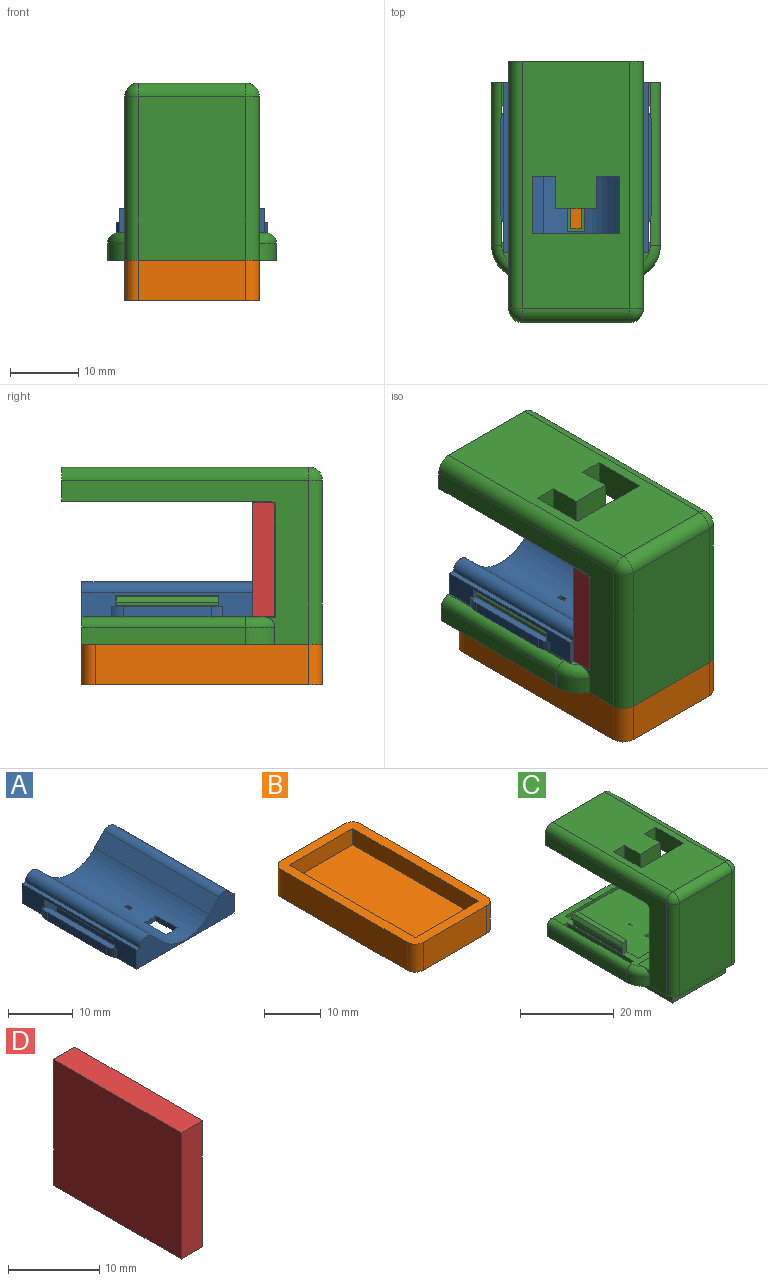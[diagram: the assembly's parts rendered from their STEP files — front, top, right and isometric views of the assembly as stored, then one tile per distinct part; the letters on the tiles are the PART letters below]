
ASSEMBLY  parts=4 mates=1
PART A: 50 faces, bbox 22.3x25x5.7 mm
  f0: plane 16.2x1.05mm, normal (0,0,1), area 15.9mm2, adj f2,f41,f42,f44,f45,f46,f47
  f1: plane 3.4x0.6mm, normal (1,0,0), area 2mm2, adj f5,f6,f13,f42
  f2: plane 25x3.64mm, normal (1,0,0), area 42.3mm2, adj f0,f6,f14,f15,f32,f40,f41,f42
  f3: plane 25x3.64mm, normal (-1,0,0), area 42.3mm2, adj f6,f14,f15,f31,f33,f34,f36,f37
  f4: plane 3.4x0.6mm, normal (-1,0,0), area 2mm2, adj f5,f6,f30,f34
  f5: plane 22x16.78mm, normal (0,0,-1), area 347.9mm2, adj f1,f4,f7,f8,f9,f10,f11,f12
  f6: plane 25x22.28mm, normal (0,0,-1), area 126.3mm2, adj f1,f2,f3,f4,f7,f8,f13,f14
  f7: plane 3.4x0.6mm, normal (-1,0,0), area 2mm2, adj f5,f6,f13,f33
  f8: plane 3.4x0.6mm, normal (1,0,0), area 2mm2, adj f5,f6,f30,f41
  f9: plane 0.55x0.39mm, normal (0,1,0), area 0.2mm2, adj f5,f10,f12,f27
  f10: plane 0.89x0.55mm, normal (-1,0,0), area 0.5mm2, adj f5,f9,f11,f27
  f11: plane 0.55x0.39mm, normal (0,-1,0), area 0.2mm2, adj f5,f10,f12,f27
  f12: plane 0.89x0.55mm, normal (1,0,0), area 0.5mm2, adj f5,f9,f11,f27
  f13: plane 16.78x0.6mm, normal (0,1,0), area 10.1mm2, adj f1,f5,f6,f7
  f14: plane 21.28x5.14mm, normal (0,1,0), area 56.1mm2, adj f2,f3,f6,f16,f17,f18,f28,f29
  f15: plane 21.28x5.14mm, normal (0,-1,0), area 56.1mm2, adj f2,f3,f6,f16,f17,f18,f28,f29
  f16: cylinder r=7mm len=25mm, axis (0,1,0), area 262.3mm2, adj f14,f15,f17,f18,f19,f20,f21,f22
  f17: plane 25x2.16mm, normal (-0.71,0,0.71), area 76.5mm2, adj f14,f15,f16,f29
  f18: plane 25x2.61mm, normal (0.71,0,0.71), area 92.1mm2, adj f14,f15,f16,f28
  f19: plane 4.7x0.97mm, normal (-1,0,0), area 4.6mm2, adj f5,f16,f20,f22
  f20: plane 2.5x0.97mm, normal (0,1,0), area 2.2mm2, adj f5,f16,f19,f21
  f21: plane 4.7x0.97mm, normal (1,0,0), area 4.6mm2, adj f5,f16,f20,f22
  f22: plane 2.5x0.97mm, normal (0,-1,0), area 2.2mm2, adj f5,f16,f19,f21
  f23: plane 1.15x0.32mm, normal (-1,0,0), area 0.4mm2, adj f16,f24,f26,f27
  f24: plane 0.65x0.32mm, normal (0,1,0), area 0.2mm2, adj f16,f23,f25,f27
  f25: plane 1.15x0.32mm, normal (1,0,0), area 0.4mm2, adj f16,f24,f26,f27
  f26: plane 0.65x0.32mm, normal (0,-1,0), area 0.2mm2, adj f16,f23,f25,f27
  f27: plane 1.15x0.65mm, normal (0,0,1), area 0.4mm2, adj f9,f10,f11,f12,f23,f24,f25,f26
  f28: cylinder r=1.5mm len=25mm, axis (0,1,0), area 88.4mm2, adj f14,f15,f18,f31
  f29: cylinder r=1.5mm len=25mm, axis (0,1,0), area 88.4mm2, adj f14,f15,f17,f32
  f30: plane 16.78x0.6mm, normal (0,-1,0), area 10.1mm2, adj f4,f5,f6,f8
  f31: plane 25x0.75mm, normal (0,0,1), area 18.8mm2, adj f3,f14,f15,f28
  f32: plane 25x0.75mm, normal (0,0,1), area 18.8mm2, adj f2,f14,f15,f29
  f33: plane 3.7x2.55mm, normal (0,-1,0), area 7.2mm2, adj f3,f5,f6,f7,f35,f36,f37,f38
  f34: plane 3.7x2.55mm, normal (0,1,0), area 7.2mm2, adj f3,f4,f5,f6,f35,f36,f37,f38
  f35: plane 15.2x1.55mm, normal (1,0,0), area 23.6mm2, adj f6,f33,f34,f37
  f36: plane 15.2x2.55mm, normal (0,0,-1), area 38.8mm2, adj f3,f33,f34,f38
  f37: plane 16.2x1.05mm, normal (0,0,1), area 15.9mm2, adj f3,f33,f34,f35,f39,f48,f49
  f38: plane 15.2x3.7mm, normal (-1,0,0), area 56.2mm2, adj f5,f33,f34,f36
  f39: plane 12.88x1.55mm, normal (-1,0,0), area 20mm2, adj f6,f37,f48,f49
  f40: plane 15.2x2.55mm, normal (0,0,-1), area 38.8mm2, adj f2,f41,f42,f43
  f41: plane 3.7x2.55mm, normal (0,1,0), area 7.2mm2, adj f0,f2,f5,f6,f8,f40,f43,f45
  f42: plane 3.7x2.55mm, normal (0,-1,0), area 7.2mm2, adj f0,f1,f2,f5,f6,f40,f43,f45
  f43: plane 15.2x3.7mm, normal (1,0,0), area 56.2mm2, adj f5,f40,f41,f42
  f44: plane 12.88x1.55mm, normal (1,0,0), area 20mm2, adj f0,f6,f46,f47
  f45: plane 15.2x1.55mm, normal (-1,0,0), area 23.6mm2, adj f0,f6,f41,f42
  f46: cylinder r=3mm len=1.66mm, axis (0,0,1), area 2.7mm2, adj f0,f2,f6,f44
  f47: cylinder r=3mm len=1.66mm, axis (0,0,1), area 2.7mm2, adj f0,f2,f6,f44
  f48: cylinder r=3mm len=1.66mm, axis (0,0,-1), area 2.7mm2, adj f3,f6,f37,f39
  f49: cylinder r=3mm len=1.66mm, axis (0,0,-1), area 2.7mm2, adj f3,f6,f37,f39
PART B: 15 faces, bbox 19.8x35.3x6 mm
  f0: plane 15.78x3.5mm, normal (0,-1,0), area 55.2mm2, adj f1,f3,f4,f5
  f1: plane 31.3x3.5mm, normal (1,0,0), area 109.6mm2, adj f0,f2,f4,f5
  f2: plane 15.78x3.5mm, normal (0,1,0), area 55.2mm2, adj f1,f3,f4,f5
  f3: plane 31.3x3.5mm, normal (-1,0,0), area 109.6mm2, adj f0,f2,f4,f5
  f4: plane 31.3x15.78mm, normal (0,0,1), area 493.9mm2, adj f0,f1,f2,f3
  f5: plane 35.3x19.78mm, normal (0,0,1), area 200.9mm2, adj f0,f1,f2,f3,f7,f8,f9,f10
  f6: plane 35.3x19.78mm, normal (0,0,-1), area 694.8mm2, adj f7,f8,f9,f10,f11,f12,f13,f14
  f7: cylinder r=2mm len=6mm, axis (0,0,1), area 18.8mm2, adj f5,f6,f11,f13
  f8: cylinder r=2mm len=6mm, axis (0,0,-1), area 18.8mm2, adj f5,f6,f10,f11
  f9: cylinder r=2mm len=6mm, axis (0,0,1), area 18.8mm2, adj f5,f6,f10,f14
  f10: plane 15.78x6mm, normal (0,-1,0), area 94.7mm2, adj f5,f6,f8,f9
  f11: plane 31.3x6mm, normal (-1,0,0), area 187.8mm2, adj f5,f6,f7,f8
  f12: cylinder r=2mm len=6mm, axis (0,0,-1), area 18.8mm2, adj f5,f6,f13,f14
  f13: plane 15.78x6mm, normal (0,1,0), area 94.7mm2, adj f5,f6,f7,f12
  f14: plane 31.3x6mm, normal (1,0,0), area 187.8mm2, adj f5,f6,f9,f12
PART C: 83 faces, bbox 26.3x39x29.7 mm
  f0: plane 5x3.39mm, normal (0,-1,0), area 17mm2, adj f15,f18,f41,f80
  f1: plane 35.3x24.78mm, normal (0,0,-1), area 297.8mm2, adj f10,f11,f12,f13,f14,f26,f27,f28
  f2: plane 26.43x10.84mm, normal (0,0,1), area 50.1mm2, adj f8,f11,f12,f17,f35,f54,f55,f56
  f3: plane 15x1.68mm, normal (1,0,0), area 25.2mm2, adj f9,f57,f58,f66
  f4: plane 1.5x0.39mm, normal (0,1,0), area 0.6mm2, adj f5,f7,f16,f25
  f5: plane 1.5x0.89mm, normal (-1,0,0), area 1.3mm2, adj f4,f6,f16,f25
  f6: plane 1.5x0.39mm, normal (0,-1,0), area 0.6mm2, adj f5,f7,f16,f25
  f7: plane 1.5x0.89mm, normal (1,0,0), area 1.3mm2, adj f4,f6,f16,f25
  f8: cylinder r=7mm len=1.5mm, axis (0,1,0), area 0.2mm2, adj f2,f9,f35,f54
  f9: plane 26.43x10.84mm, normal (0,0,1), area 50.1mm2, adj f3,f8,f12,f14,f17,f35,f53,f54
  f10: plane 36.95x24.65mm, normal (-1,0,0), area 214.7mm2, adj f1,f18,f24,f35,f36,f47,f49,f50
  f11: plane 20x4mm, normal (-1,0,0), area 80mm2, adj f1,f2,f70,f76
  f12: plane 24.78x4mm, normal (0,1,0), area 98.2mm2, adj f1,f2,f9,f17,f51,f52,f74,f78
  f13: plane 36.95x24.65mm, normal (1,0,0), area 214.7mm2, adj f1,f18,f24,f35,f36,f44,f46,f50
  f14: plane 20x4mm, normal (1,0,0), area 80mm2, adj f1,f9,f71,f77
  f15: plane 36.3x15.78mm, normal (0,0,1), area 494.2mm2, adj f0,f37,f40,f41,f42,f43,f46,f49
  f16: plane 24x11.78mm, normal (0,0,-1), area 276.8mm2, adj f4,f5,f6,f7,f20,f21,f22,f23
  f17: cylinder r=7mm len=1.5mm, axis (0,1,0), area 0.2mm2, adj f2,f9,f12,f55
  f18: plane 30.3x19.78mm, normal (0,0,-1), area 520.8mm2, adj f0,f10,f13,f36,f40,f41,f42,f43
  f19: plane 31.3x15.78mm, normal (0,0,-1), area 211.2mm2, adj f26,f27,f28,f29,f30,f31,f32,f34
  f20: plane 1.5x1.5mm, normal (0,1,0), area 2.2mm2, adj f16,f21,f23,f25
  f21: plane 3.7x1.5mm, normal (1,0,0), area 5.5mm2, adj f16,f20,f22,f25
  f22: plane 1.5x1.5mm, normal (0,-1,0), area 2.2mm2, adj f16,f21,f23,f25
  f23: plane 3.7x1.5mm, normal (-1,0,0), area 5.5mm2, adj f16,f20,f22,f25
  f24: plane 19.78x16mm, normal (0,1,0), area 316.3mm2, adj f10,f13,f35,f36
  f25: plane 22x16.78mm, normal (0,0,1), area 363.3mm2, adj f4,f5,f6,f7,f20,f21,f22,f23
  f26: plane 31.3x3mm, normal (-1,0,0), area 93.9mm2, adj f1,f19,f28,f34
  f27: plane 31.3x3mm, normal (1,0,0), area 93.9mm2, adj f1,f19,f28,f34
  f28: plane 15.78x3mm, normal (0,1,0), area 47.3mm2, adj f1,f19,f26,f27
  f29: plane 11.78x4.74mm, normal (0,1,0), area 55.8mm2, adj f16,f19,f30,f32
  f30: plane 24x4.74mm, normal (1,0,0), area 113.8mm2, adj f16,f19,f29,f31
  f31: plane 11.78x4.74mm, normal (0,-1,0), area 55.8mm2, adj f16,f19,f30,f32
  f32: plane 24x4.74mm, normal (-1,0,0), area 113.8mm2, adj f16,f19,f29,f31
  f33: plane 24x15.78mm, normal (0,-1,0), area 378.7mm2, adj f1,f37,f44,f47
  f34: plane 15.78x3mm, normal (0,-1,0), area 47.3mm2, adj f1,f19,f26,f27
  f35: plane 19.79x3.31mm, normal (0,0,1), area 65.3mm2, adj f2,f8,f9,f10,f13,f24
  f36: cylinder r=1mm len=19.78mm, axis (-1,0,0), area 31.1mm2, adj f10,f13,f18,f24
  f37: cylinder r=2mm len=15.78mm, axis (-1,0,0), area 49.6mm2, adj f15,f33,f45,f48
  f38: plane 20x4mm, normal (-1,0,0), area 80mm2, adj f1,f71,f74,f77
  f39: plane 20x4mm, normal (1,0,0), area 80mm2, adj f1,f70,f76,f78
  f40: plane 5x3.39mm, normal (0,-1,0), area 16.9mm2, adj f15,f18,f43,f82
  f41: plane 8.33x5mm, normal (1,0,0), area 41.7mm2, adj f0,f15,f18,f42
  f42: plane 12.78x5mm, normal (0,1,0), area 63.9mm2, adj f15,f18,f41,f43
  f43: plane 8.33x5mm, normal (-1,0,0), area 41.7mm2, adj f15,f18,f40,f42
  f44: cylinder r=2mm len=24mm, axis (0,0,-1), area 75.4mm2, adj f1,f13,f33,f45
  f45: sphere r=2mm, area 6.3mm2, adj f37,f44,f46
  f46: cylinder r=2mm len=36.3mm, axis (0,-1,0), area 114mm2, adj f13,f15,f45,f50
  f47: cylinder r=2mm len=24mm, axis (0,0,1), area 75.4mm2, adj f1,f10,f33,f48
  f48: sphere r=2mm, area 6.3mm2, adj f37,f47,f49
  f49: cylinder r=2mm len=36.3mm, axis (0,1,0), area 114mm2, adj f10,f15,f48,f50
  f50: plane 19.78x5mm, normal (0,1,0), area 97.2mm2, adj f10,f13,f15,f18,f46,f49
  f51: plane 23.97x2.5mm, normal (1,0,0), area 59.9mm2, adj f1,f12,f73,f74
  f52: plane 23.97x2.5mm, normal (-1,0,0), area 59.9mm2, adj f1,f12,f72,f78
  f53: plane 22x3.76mm, normal (-1,0,0), area 61.7mm2, adj f9,f25,f54,f55,f57,f58,f59
  f54: plane 16.78x0.76mm, normal (0,1,0), area 12.8mm2, adj f2,f8,f9,f25,f53,f56
  f55: plane 16.78x0.76mm, normal (0,-1,0), area 12.8mm2, adj f2,f9,f17,f25,f53,f56
  f56: plane 22x3.76mm, normal (1,0,0), area 61.7mm2, adj f2,f25,f54,f55,f60,f62,f63
  f57: plane 3x1.77mm, normal (0,-1,0), area 4.1mm2, adj f3,f9,f53,f59,f64,f65,f66
  f58: plane 3x1.77mm, normal (0,1,0), area 4.1mm2, adj f3,f9,f53,f59,f64,f65,f66
  f59: plane 15x1.2mm, normal (0,0,1), area 18mm2, adj f53,f57,f58,f64
  f60: plane 3x1.77mm, normal (0,1,0), area 4.1mm2, adj f2,f56,f61,f63,f67,f68,f69
  f61: plane 15x1.68mm, normal (-1,0,0), area 25.2mm2, adj f2,f60,f62,f68
  f62: plane 3x1.77mm, normal (0,-1,0), area 4.1mm2, adj f2,f56,f61,f63,f67,f68,f69
  f63: plane 15x1.2mm, normal (0,0,1), area 18mm2, adj f56,f60,f62,f67
  f64: plane 15x0.82mm, normal (0.82,0,0.57), area 15mm2, adj f57,f58,f59,f65
  f65: plane 15x0.5mm, normal (1,0,0), area 7.5mm2, adj f57,f58,f64,f66
  f66: plane 15x0.57mm, normal (0,0,-1), area 8.6mm2, adj f3,f57,f58,f65
  f67: plane 15x0.82mm, normal (-0.82,0,0.57), area 15mm2, adj f60,f62,f63,f69
  f68: plane 15x0.57mm, normal (0,0,-1), area 8.6mm2, adj f60,f61,f62,f69
  f69: plane 15x0.5mm, normal (-1,0,0), area 7.5mm2, adj f60,f62,f67,f68
  f70: plane 4x1mm, normal (0,1,0), area 4mm2, adj f1,f2,f11,f39
  f71: plane 4x1mm, normal (0,1,0), area 4mm2, adj f1,f9,f14,f38
  f72: cylinder r=5mm len=4.33mm, axis (0,0,1), area 13.1mm2, adj f1,f10,f52,f79
  f73: cylinder r=5mm len=4.33mm, axis (0,0,-1), area 13.1mm2, adj f1,f13,f51,f75
  f74: cylinder r=1.5mm len=23.97mm, axis (0,1,0), area 56.5mm2, adj f9,f12,f38,f51,f75
  f75: torus R=3.5mm, axis (0,0,-1), area 9.6mm2, adj f9,f13,f73,f74
  f76: plane 4x1mm, normal (0,-1,0), area 4mm2, adj f1,f2,f11,f39
  f77: plane 4x1mm, normal (0,-1,0), area 4mm2, adj f1,f9,f14,f38
  f78: cylinder r=1.5mm len=23.97mm, axis (0,-1,0), area 56.5mm2, adj f2,f12,f39,f52,f79
  f79: torus R=3.5mm, axis (0,0,1), area 9.6mm2, adj f2,f10,f72,f78
  f80: plane 5x4.65mm, normal (-1,0,0), area 23.3mm2, adj f0,f15,f18,f81
  f81: plane 6x5mm, normal (0,-1,0), area 30mm2, adj f15,f18,f80,f82
  f82: plane 5x4.65mm, normal (1,0,0), area 23.3mm2, adj f15,f18,f40,f81
PART D: 6 faces, bbox 3.3x19.8x16.9 mm
  f0: plane 19.78x3.3mm, normal (0,0,1), area 65.3mm2, adj f1,f3,f4,f5
  f1: plane 19.78x16.9mm, normal (-1,0,0), area 334.3mm2, adj f0,f2,f4,f5
  f2: plane 19.78x3.3mm, normal (0,0,-1), area 65.3mm2, adj f1,f3,f4,f5
  f3: plane 19.78x16.9mm, normal (1,0,0), area 334.3mm2, adj f0,f2,f4,f5
  f4: plane 16.9x3.3mm, normal (0,-1,0), area 55.8mm2, adj f0,f1,f2,f3
  f5: plane 16.9x3.3mm, normal (0,1,0), area 55.8mm2, adj f0,f1,f2,f3
PLACE A rot(axis=(0,-1,0),0deg) t=(3.47,22.7,-5.21)mm
PLACE B rot(axis=(0,-1,0),0deg) t=(12.19,6.89,-8.47)mm fixed
PLACE C rot(axis=(0,-1,0),0deg) t=(3.47,22.7,-5.47)mm fixed
PLACE D rot(axis=(0,0,1),90deg) t=(3.42,-2.18,4.39)mm
MATE slider A.f5 <-> C.f25  axis (0,0,-1) through (13.09,9.53,0.93)mm
